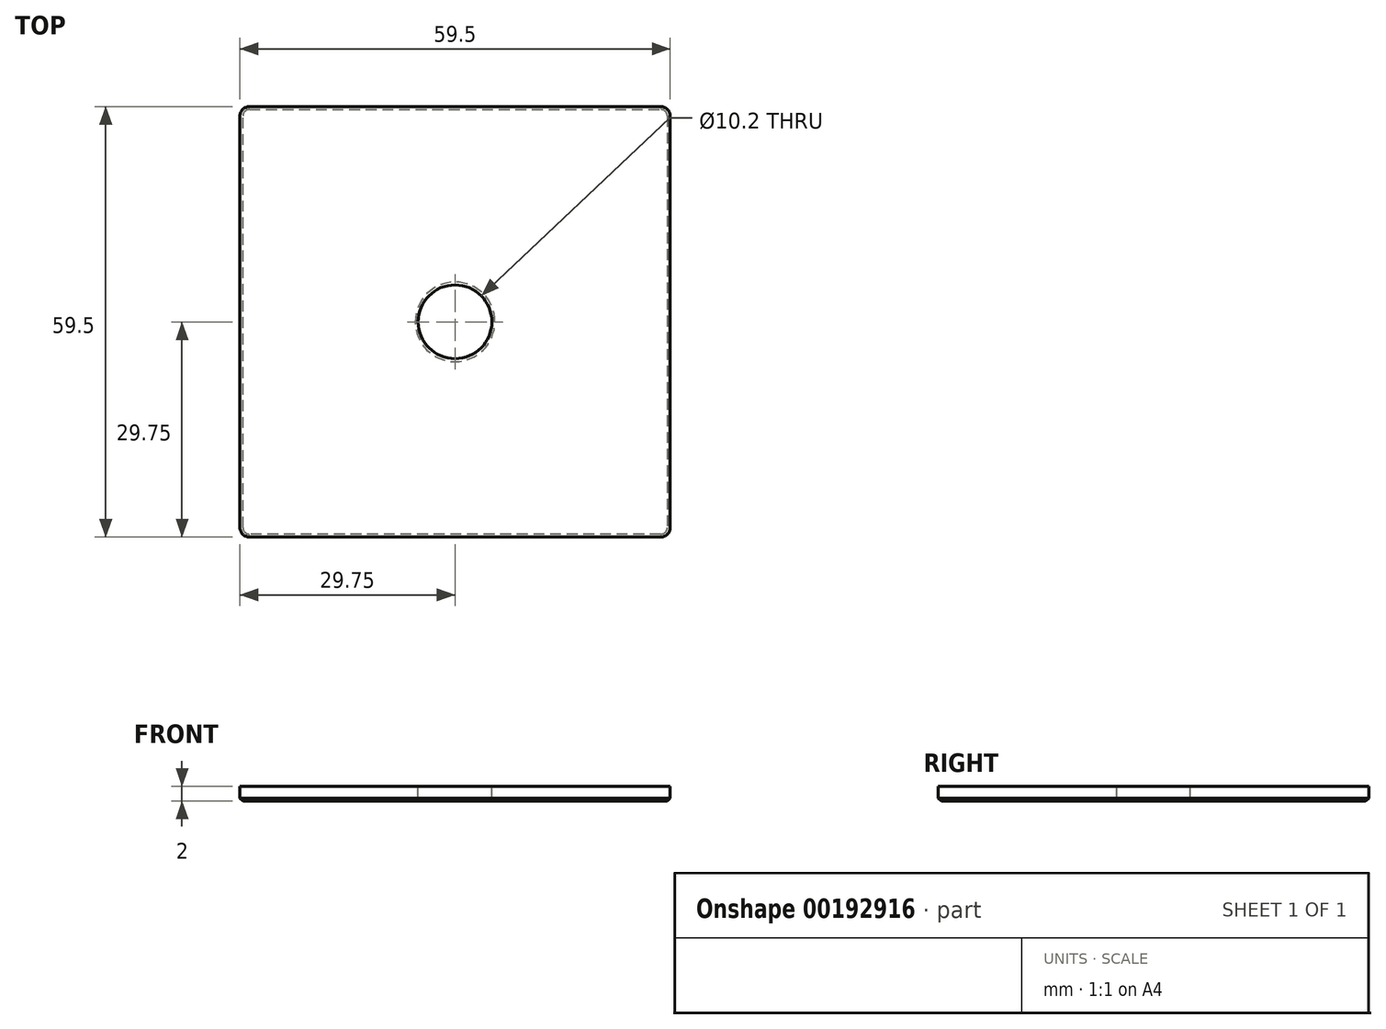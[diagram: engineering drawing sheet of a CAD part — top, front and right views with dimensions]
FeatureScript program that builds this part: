
annotation { "Feature Type Name" : "Feature", "Feature Type Description" : "" }
export const myFeature = defineFeature(function(context is Context, id is Id, definition is map)
    precondition{}
    {
        {
            var Q0;
            Q0=qCreatedBy(makeId("Top.planeOp"),FACE);
            var sketch = newSketch(context, id + "F0", { "sketchPlane" : qUnion([Q0])});
            skLineSegment(sketch, "E0.bottom", {"start": v(29.75, -29.75) * mm, "end": v(-29.75, -29.75) * mm});
            skLineSegment(sketch, "E0.top", {"start": v(29.75, 29.75) * mm, "end": v(-29.75, 29.75) * mm});
            skLineSegment(sketch, "E0.left", {"start": v(29.75, -29.75) * mm, "end": v(29.75, 29.75) * mm});
            skLineSegment(sketch, "E0.right", {"start": v(-29.75, -29.75) * mm, "end": v(-29.75, 29.75) * mm});
            skPoint(sketch, "E0.middle", {"position": v(0, 0) * mm});
            skSolve(sketch);
        }
        {
            var Q0;
            Q0 = qSketchRegion(id + "F0", true);
            extrude(context, id + "F1", {"entities" : qUnion([Q0]), "depth" : 2 * mm});
        }
        {
            var Q0;
            Q0=makeQuery(id+"F1.opExtrude","SWEPT_EDGE",EDGE,{"disambiguationData":[OSD([sQuery(id+"F0.wireOp",EDGE,"E0.bottom"),sQuery(id+"F0.wireOp",EDGE,"E0.left")])]});
            var Q1;
            Q1=makeQuery(id+"F1.opExtrude","SWEPT_EDGE",EDGE,{"disambiguationData":[OSD([sQuery(id+"F0.wireOp",EDGE,"E0.bottom"),sQuery(id+"F0.wireOp",EDGE,"E0.right")])]});
            var Q2;
            Q2=makeQuery(id+"F1.opExtrude","SWEPT_EDGE",EDGE,{"disambiguationData":[OSD([sQuery(id+"F0.wireOp",EDGE,"E0.top"),sQuery(id+"F0.wireOp",EDGE,"E0.left")])]});
            var Q3;
            Q3=makeQuery(id+"F1.opExtrude","SWEPT_EDGE",EDGE,{"disambiguationData":[OSD([sQuery(id+"F0.wireOp",EDGE,"E0.top"),sQuery(id+"F0.wireOp",EDGE,"E0.right")])]});
            fillet(context, id + "F2", {"entities" : qUnion([Q0, Q1, Q2, Q3]), "radius" : 1.3 * mm, "tangentPropagation" : true, "allowEdgeOverflow" : false});
        }
        {
            var Q0;
            Q0=makeQuery(id+"F1.opExtrude","CAP_FACE",FACE,{"disambiguationData":[OSD([sQuery(id+"F0.wireOp",EDGE,"E0.bottom"),sQuery(id+"F0.wireOp",EDGE,"E0.top"),sQuery(id+"F0.wireOp",EDGE,"E0.left"),sQuery(id+"F0.wireOp",EDGE,"E0.right")])],"isStart":false});
            var sketch = newSketch(context, id + "F3", { "sketchPlane" : qUnion([Q0])});
            skCircle(sketch, "E1", {"center": v(0, 0) * mm, "radius": 5.1 * mm});
            skSolve(sketch);
        }
        {
            var Q0;
            Q0 = qSketchRegion(id + "F3", true);
            extrude(context, id + "F4", {"entities" : qUnion([Q0]), "operationType" : NewBodyOperationType.REMOVE, "oppositeDirection" : true, "depth" : 25 * mm});
        }
        {
            var Q0;
            Q0=makeQuery(id+"F1.opExtrude","CAP_EDGE",EDGE,{"disambiguationData":[OSD([sQuery(id+"F0.wireOp",EDGE,"E0.bottom")])],"isStart":true});
            var Q1;
            Q1=makeQuery(id+"F4.boolean.opBoolean","COPY",EDGE,{"derivedFrom":makeQuery(id+"F4.opExtrude","CAP_EDGE",EDGE,{"disambiguationData":[OSD([sQuery(id+"F3.wireOp",EDGE,"E1")])],"isStart":true})});
            var Q2;
            Q2=makeQuery(id+"F4.boolean.opBoolean","INTERSECT",EDGE,{"derivedFrom":[makeQuery(id+"F1.opExtrude","CAP_FACE",FACE,{"disambiguationData":[OSD([sQuery(id+"F0.wireOp",EDGE,"E0.bottom"),sQuery(id+"F0.wireOp",EDGE,"E0.top"),sQuery(id+"F0.wireOp",EDGE,"E0.left"),sQuery(id+"F0.wireOp",EDGE,"E0.right")])],"isStart":true}),makeQuery(id+"F4.opExtrude","SWEPT_FACE",FACE,{"disambiguationData":[OSD([sQuery(id+"F3.wireOp",EDGE,"E1")])]})]});
            chamfer(context, id + "F5", {"entities" : qUnion([Q0, Q1, Q2]), "width" : 0.4 * mm, "tangentPropagation" : true});
        }
    });
